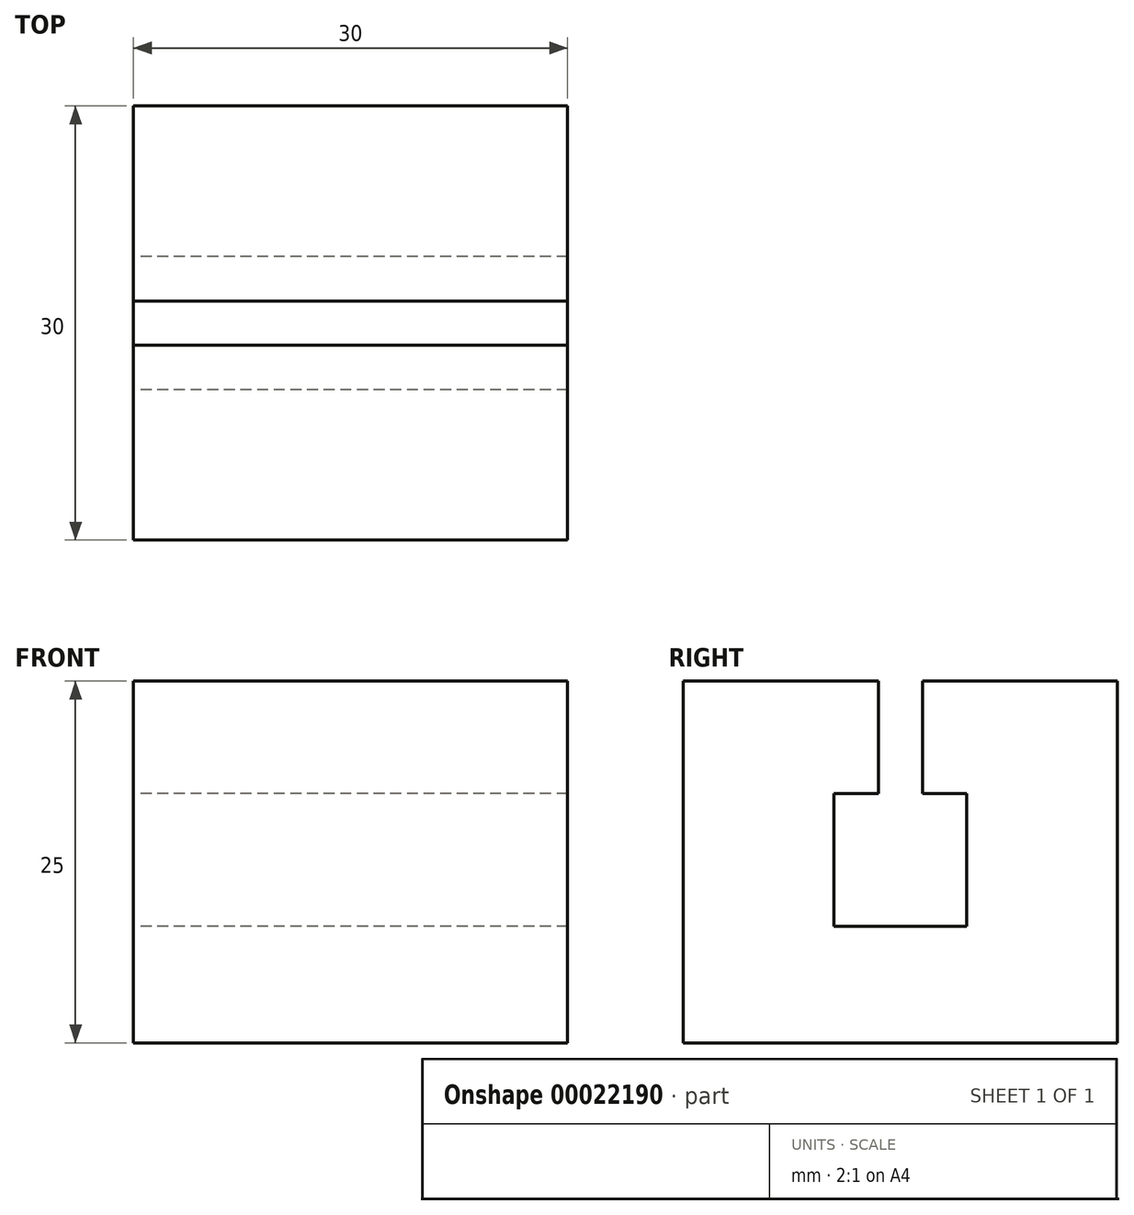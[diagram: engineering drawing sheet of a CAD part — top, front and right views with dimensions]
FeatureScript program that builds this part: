
annotation { "Feature Type Name" : "Feature", "Feature Type Description" : "" }
export const myFeature = defineFeature(function(context is Context, id is Id, definition is map)
    precondition{}
    {
        {
            var Q0;
            Q0=qCreatedBy(makeId("Right.planeOp"),FACE);
            var sketch = newSketch(context, id + "F0", { "sketchPlane" : qUnion([Q0])});
            skLineSegment(sketch, "E0.rect.bottom", {"start": v(15, -12.5) * mm, "end": v(-15, -12.5) * mm});
            skLineSegment(sketch, "E0.rect.top", {"start": v(15, 12.5) * mm, "end": v(1.52, 12.5) * mm});
            skLineSegment(sketch, "E0.rect.left", {"start": v(15, -12.5) * mm, "end": v(15, 12.5) * mm});
            skLineSegment(sketch, "E0.rect.right", {"start": v(-15, -12.5) * mm, "end": v(-15, 12.5) * mm});
            skPoint(sketch, "E0.rect.middle", {"position": v(0, 0) * mm});
            skLineSegment(sketch, "E1.rect.top", {"start": v(1.53, -4.46) * mm, "end": v(-1.53, -4.46) * mm});
            skLineSegment(sketch, "E1.rect.left", {"start": v(1.53, 12.5) * mm, "end": v(1.52, 4.74) * mm});
            skLineSegment(sketch, "E1.rect.right", {"start": v(-1.52, 12.5) * mm, "end": v(-1.53, 4.74) * mm});
            skPoint(sketch, "E1.rect.middle", {"position": v(0, 4.02) * mm});
            skLineSegment(sketch, "E2.bottom", {"start": v(-1.53, -4.46) * mm, "end": v(-4.6, -4.46) * mm});
            skLineSegment(sketch, "E2.top", {"start": v(-1.53, 4.74) * mm, "end": v(-4.6, 4.74) * mm});
            skLineSegment(sketch, "E2.right", {"start": v(-4.6, -4.46) * mm, "end": v(-4.6, 4.74) * mm});
            skLineSegment(sketch, "E3", {"start": v(0, -17.78) * mm, "end": v(0, 21.45) * mm, "construction": true});
            skLineSegment(sketch, "E4.MirrorCS", {"start": v(1.53, -4.46) * mm, "end": v(4.6, -4.46) * mm});
            skLineSegment(sketch, "E5.MirrorCS", {"start": v(4.6, -4.46) * mm, "end": v(4.6, 4.74) * mm});
            skLineSegment(sketch, "E6.MirrorCS", {"start": v(1.53, 4.74) * mm, "end": v(4.6, 4.74) * mm});
            skPoint(sketch, "E7.MirrorCS.end.orphan", {"position": v(1.53, 4.74) * mm});
            skPoint(sketch, "E7.MirrorCS.start.orphan", {"position": v(1.53, -4.46) * mm});
            skLineSegment(sketch, "E8.trimOffspring", {"start": v(-1.52, 12.5) * mm, "end": v(-15, 12.5) * mm});
            skSolve(sketch);
        }
        {
            var Q0;
            Q0 = qSketchRegion(id + "F0", true);
            extrude(context, id + "F1", {"entities" : qUnion([Q0]), "depth" : 30 * mm});
        }
    });
